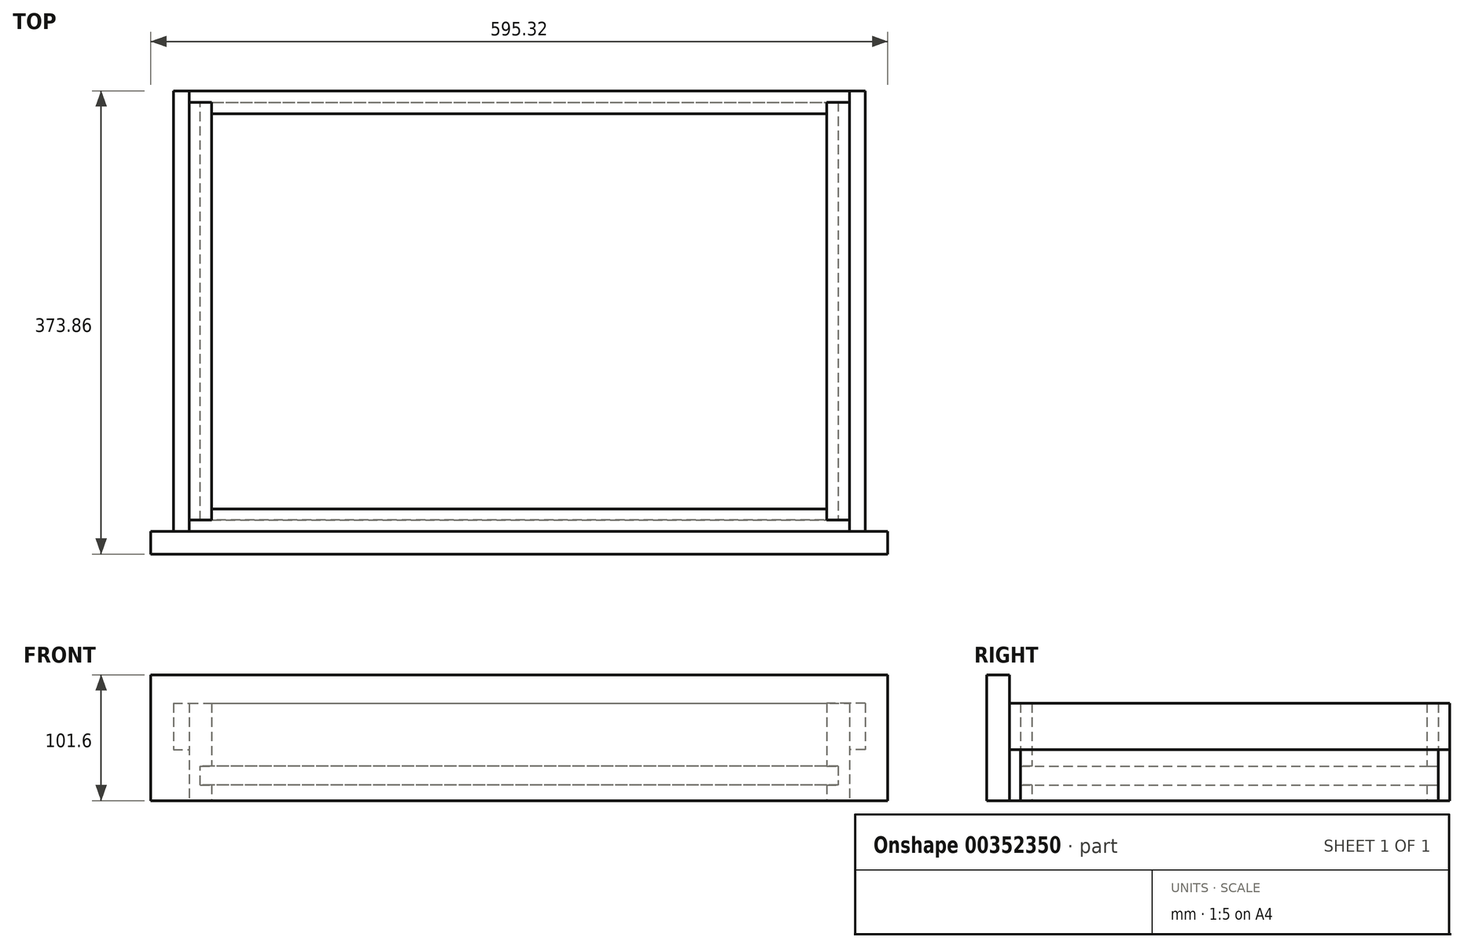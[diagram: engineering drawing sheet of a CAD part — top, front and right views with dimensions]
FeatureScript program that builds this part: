
annotation { "Feature Type Name" : "Feature", "Feature Type Description" : "" }
export const myFeature = defineFeature(function(context is Context, id is Id, definition is map)
    precondition{}
    {
        {
            var Q0;
            Q0=qCreatedBy(makeId("Top.planeOp"),FACE);
            var sketch = newSketch(context, id + "F0", { "sketchPlane" : qUnion([Q0])});
            skLineSegment(sketch, "E0.top", {"start": v(-266.7, -177.8) * mm, "end": v(266.7, -177.8) * mm, "construction": true});
            skLineSegment(sketch, "E0.left", {"start": v(-266.7, -177.8) * mm, "end": v(-266.7, 177.8) * mm, "construction": true});
            skLineSegment(sketch, "E0.right", {"start": v(266.7, -177.8) * mm, "end": v(266.7, 177.8) * mm, "construction": true});
            skLineSegment(sketch, "E1", {"start": v(-266.7, 177.8) * mm, "end": v(266.7, 177.8) * mm, "construction": true});
            skLineSegment(sketch, "E2", {"start": v(-266.7, 177.8) * mm, "end": v(-266.7, 168.67) * mm});
            skLineSegment(sketch, "E3", {"start": v(-266.7, 168.67) * mm, "end": v(-248.44, 168.67) * mm});
            skLineSegment(sketch, "E4", {"start": v(-248.44, 168.67) * mm, "end": v(-248.44, 159.54) * mm});
            skLineSegment(sketch, "E5.MirrorCS", {"start": v(266.7, 177.8) * mm, "end": v(266.7, 168.67) * mm});
            skLineSegment(sketch, "E6.MirrorCS", {"start": v(248.44, 168.67) * mm, "end": v(248.44, 159.54) * mm});
            skLineSegment(sketch, "E7.MirrorCS", {"start": v(266.7, 168.67) * mm, "end": v(248.44, 168.67) * mm});
            skLineSegment(sketch, "E8", {"start": v(-266.7, 177.8) * mm, "end": v(266.7, 177.8) * mm});
            skLineSegment(sketch, "E9", {"start": v(-248.44, 159.54) * mm, "end": v(248.44, 159.54) * mm});
            skLineSegment(sketch, "E10.MirrorCS", {"start": v(266.7, -177.8) * mm, "end": v(266.7, -168.67) * mm});
            skLineSegment(sketch, "E11.MirrorCS", {"start": v(-266.7, -177.8) * mm, "end": v(-266.7, -168.67) * mm});
            skLineSegment(sketch, "E12.MirrorCS", {"start": v(248.44, -168.67) * mm, "end": v(248.44, -159.54) * mm});
            skLineSegment(sketch, "E13.MirrorCS", {"start": v(266.7, -168.67) * mm, "end": v(248.44, -168.67) * mm});
            skLineSegment(sketch, "E14.MirrorCS", {"start": v(-248.44, -168.67) * mm, "end": v(-248.44, -159.54) * mm});
            skLineSegment(sketch, "E15.MirrorCS", {"start": v(-266.7, -168.67) * mm, "end": v(-248.44, -168.67) * mm});
            skLineSegment(sketch, "E16.MirrorCS", {"start": v(-266.7, -177.8) * mm, "end": v(266.7, -177.8) * mm});
            skLineSegment(sketch, "E17.MirrorCS", {"start": v(-248.44, -159.54) * mm, "end": v(248.44, -159.54) * mm});
            skLineSegment(sketch, "E18", {"start": v(-297.66, 177.8) * mm, "end": v(-297.66, -177.8) * mm, "construction": true});
            skLineSegment(sketch, "E19.MirrorCS", {"start": v(297.66, 177.8) * mm, "end": v(297.66, -177.8) * mm, "construction": true});
            skSolve(sketch);
        }
        {
            var Q0;
            Q0=qCreatedBy(makeId("Top.planeOp"),FACE);
            var sketch = newSketch(context, id + "F1", { "sketchPlane" : qUnion([Q0])});
            skLineSegment(sketch, "E20.bottom", {"start": v(-266.7, 168.67) * mm, "end": v(-248.44, 168.67) * mm});
            skLineSegment(sketch, "E20.top", {"start": v(-266.7, -168.67) * mm, "end": v(-248.44, -168.67) * mm});
            skLineSegment(sketch, "E20.left", {"start": v(-266.7, 168.67) * mm, "end": v(-266.7, -168.67) * mm});
            skLineSegment(sketch, "E20.right", {"start": v(-248.44, 168.67) * mm, "end": v(-248.44, -168.67) * mm});
            skLineSegment(sketch, "E21.MirrorCS", {"start": v(248.44, 168.67) * mm, "end": v(248.44, -168.67) * mm});
            skLineSegment(sketch, "E22.MirrorCS", {"start": v(266.7, 168.67) * mm, "end": v(266.7, -168.67) * mm});
            skLineSegment(sketch, "E23.MirrorCS", {"start": v(266.7, 168.67) * mm, "end": v(248.44, 168.67) * mm});
            skLineSegment(sketch, "E24.MirrorCS", {"start": v(266.7, -168.67) * mm, "end": v(248.44, -168.67) * mm});
            skSolve(sketch);
        }
        {
            var Q0;
            Q0=qCreatedBy(makeId("Top.planeOp"),FACE);
            var sketch = newSketch(context, id + "F2", { "sketchPlane" : qUnion([Q0])});
            skLineSegment(sketch, "E25.bottom", {"start": v(-297.66, -196.06) * mm, "end": v(297.66, -196.06) * mm});
            skLineSegment(sketch, "E25.top", {"start": v(-297.66, -177.8) * mm, "end": v(297.66, -177.8) * mm});
            skLineSegment(sketch, "E25.left", {"start": v(-297.66, -196.06) * mm, "end": v(-297.66, -177.8) * mm});
            skLineSegment(sketch, "E25.right", {"start": v(297.66, -196.06) * mm, "end": v(297.66, -177.8) * mm});
            skSolve(sketch);
        }
        {
            var Q0;
            Q0=qCreatedBy(makeId("Front.planeOp"),FACE);
            var sketch = newSketch(context, id + "F3", { "sketchPlane" : qUnion([Q0])});
            skLineSegment(sketch, "E26.bottom", {"start": v(-257.57, 27.78) * mm, "end": v(257.57, 27.78) * mm});
            skLineSegment(sketch, "E26.top", {"start": v(-257.57, 12.7) * mm, "end": v(257.57, 12.7) * mm});
            skLineSegment(sketch, "E26.left", {"start": v(-257.57, 27.78) * mm, "end": v(-257.57, 12.7) * mm});
            skLineSegment(sketch, "E26.right", {"start": v(257.57, 27.78) * mm, "end": v(257.57, 12.7) * mm});
            skSolve(sketch);
        }
        {
            var Q0;
            Q0=qCreatedBy(makeId("Front.planeOp"),FACE);
            var sketch = newSketch(context, id + "F4", { "sketchPlane" : qUnion([Q0])});
            skLineSegment(sketch, "E27.bottom", {"start": v(-279.4, 78.58) * mm, "end": v(-266.7, 78.58) * mm});
            skLineSegment(sketch, "E27.top", {"start": v(-279.4, 41.28) * mm, "end": v(-266.7, 41.28) * mm});
            skLineSegment(sketch, "E27.left", {"start": v(-279.4, 78.58) * mm, "end": v(-279.4, 41.28) * mm});
            skLineSegment(sketch, "E27.right", {"start": v(-266.7, 78.58) * mm, "end": v(-266.7, 41.28) * mm});
            skLineSegment(sketch, "E28.MirrorCS", {"start": v(279.4, 41.28) * mm, "end": v(266.7, 41.28) * mm});
            skLineSegment(sketch, "E29.MirrorCS", {"start": v(279.4, 78.58) * mm, "end": v(266.7, 78.58) * mm});
            skLineSegment(sketch, "E30.MirrorCS", {"start": v(279.4, 78.58) * mm, "end": v(279.4, 41.28) * mm});
            skLineSegment(sketch, "E31.MirrorCS", {"start": v(266.7, 78.58) * mm, "end": v(266.7, 41.28) * mm});
            skSolve(sketch);
        }
        {
            var Q0;
            Q0=makeQuery(id+"F0.imprint","IMPRINT",FACE,{"disambiguationData":[TD([[makeQuery(id+"F0.imprint","IMPRINT",EDGE,{"derivedFrom":sQuery(id+"F0.wireOp",EDGE,"E2")}),1.0]])]});
            var Q1;
            Q1=makeQuery(id+"F0.imprint","IMPRINT",FACE,{"disambiguationData":[TD([[makeQuery(id+"F0.imprint","IMPRINT",EDGE,{"derivedFrom":sQuery(id+"F0.wireOp",EDGE,"E10.MirrorCS")}),1.0]])]});
            extrude(context, id + "F5", {"entities" : qUnion([Q0, Q1]), "depth" : 78.58 * mm});
        }
        {
            var Q0;
            Q0=makeQuery(id+"F1.imprint","IMPRINT",FACE,{"disambiguationData":[TD([[makeQuery(id+"F1.imprint","IMPRINT",EDGE,{"derivedFrom":sQuery(id+"F1.wireOp",EDGE,"E20.bottom")}),-1.0]])]});
            var Q1;
            Q1=makeQuery(id+"F1.imprint","IMPRINT",FACE,{"disambiguationData":[TD([[makeQuery(id+"F1.imprint","IMPRINT",EDGE,{"derivedFrom":sQuery(id+"F1.wireOp",EDGE,"E21.MirrorCS")}),1.0]])]});
            var Q2;
            Q2=makeQuery(id+"F5.opExtrude","CAP_FACE",FACE,{"disambiguationData":[OSD([sQuery(id+"F0.wireOp",EDGE,"E2"),sQuery(id+"F0.wireOp",EDGE,"E3"),sQuery(id+"F0.wireOp",EDGE,"E4"),sQuery(id+"F0.wireOp",EDGE,"E5.MirrorCS"),sQuery(id+"F0.wireOp",EDGE,"E6.MirrorCS"),sQuery(id+"F0.wireOp",EDGE,"E7.MirrorCS"),sQuery(id+"F0.wireOp",EDGE,"E8"),sQuery(id+"F0.wireOp",EDGE,"E9")])],"isStart":false});
            extrude(context, id + "F6", {"entities" : qUnion([Q0, Q1]), "endBound" : BoundingType.UP_TO_SURFACE, "endBoundEntityFace" : qUnion([Q2]), "depth" : 228.6 * mm});
        }
        {
            var Q0;
            Q0=makeQuery(id+"F2.imprint","IMPRINT",FACE,{"disambiguationData":[TD([[makeQuery(id+"F2.imprint","IMPRINT",EDGE,{"derivedFrom":sQuery(id+"F2.wireOp",EDGE,"E25.bottom")}),1.0]])]});
            extrude(context, id + "F7", {"entities" : qUnion([Q0]), "depth" : 101.6 * mm});
        }
        {
            var Q0;
            Q0 = qSketchRegion(id + "F3", true);
            var Q1;
            Q1=makeQuery(id+"F5.opExtrude","SWEPT_FACE",FACE,{"disambiguationData":[OSD([sQuery(id+"F0.wireOp",EDGE,"E13.MirrorCS")])]});
            var Q2;
            Q2=makeQuery(id+"F5.opExtrude","SWEPT_FACE",FACE,{"disambiguationData":[OSD([sQuery(id+"F0.wireOp",EDGE,"E7.MirrorCS")])]});
            extrude(context, id + "F8", {"entities" : qUnion([Q0]), "operationType" : NewBodyOperationType.REMOVE, "oppositeDirection" : true, "endBoundEntityFace" : qUnion([Q1]), "depth" : 168.67 * mm, "hasSecondDirection" : true, "secondDirectionOppositeDirection" : false, "secondDirectionBoundEntityFace" : qUnion([Q2]), "secondDirectionDepth" : 168.67 * mm});
        }
        {
            var Q0;
            Q0 = qSketchRegion(id + "F3", true);
            var Q1;
            Q1=makeQuery(id+"F8.boolean.opBoolean","MERGE",FACE,{"derivedFrom":[makeQuery(id+"F5.opExtrude","SWEPT_FACE",FACE,{"disambiguationData":[OSD([sQuery(id+"F0.wireOp",EDGE,"E13.MirrorCS")])]}),makeQuery(id+"F5.opExtrude","SWEPT_FACE",FACE,{"disambiguationData":[OSD([sQuery(id+"F0.wireOp",EDGE,"E15.MirrorCS")])]}),makeQuery(id+"F8.opExtrude","CAP_FACE",FACE,{"disambiguationData":[OSD([sQuery(id+"F3.wireOp",EDGE,"E26.bottom"),sQuery(id+"F3.wireOp",EDGE,"E26.top"),sQuery(id+"F3.wireOp",EDGE,"E26.left"),sQuery(id+"F3.wireOp",EDGE,"E26.right")])],"isStart":true})]});
            var Q2;
            Q2=makeQuery(id+"F8.boolean.opBoolean","MERGE",FACE,{"derivedFrom":[makeQuery(id+"F5.opExtrude","SWEPT_FACE",FACE,{"disambiguationData":[OSD([sQuery(id+"F0.wireOp",EDGE,"E3")])]}),makeQuery(id+"F5.opExtrude","SWEPT_FACE",FACE,{"disambiguationData":[OSD([sQuery(id+"F0.wireOp",EDGE,"E7.MirrorCS")])]}),makeQuery(id+"F8.opExtrude","CAP_FACE",FACE,{"disambiguationData":[OSD([sQuery(id+"F3.wireOp",EDGE,"E26.bottom"),sQuery(id+"F3.wireOp",EDGE,"E26.top"),sQuery(id+"F3.wireOp",EDGE,"E26.left"),sQuery(id+"F3.wireOp",EDGE,"E26.right")])],"isStart":false})]});
            extrude(context, id + "F9", {"entities" : qUnion([Q0]), "endBound" : BoundingType.UP_TO_SURFACE, "endBoundEntityFace" : qUnion([Q1]), "depth" : 25.4 * mm, "hasSecondDirection" : true, "secondDirectionBound" : SecondDirectionBoundingType.UP_TO_SURFACE, "secondDirectionOppositeDirection" : true, "secondDirectionBoundEntityFace" : qUnion([Q2]), "secondDirectionDepth" : 25.4 * mm});
        }
        {
            var Q0;
            Q0 = qSketchRegion(id + "F4", true);
            extrude(context, id + "F10", {"entities" : qUnion([Q0]), "depth" : 177.8 * mm, "hasSecondDirection" : true, "secondDirectionOppositeDirection" : true, "secondDirectionDepth" : 177.8 * mm});
        }
    });
